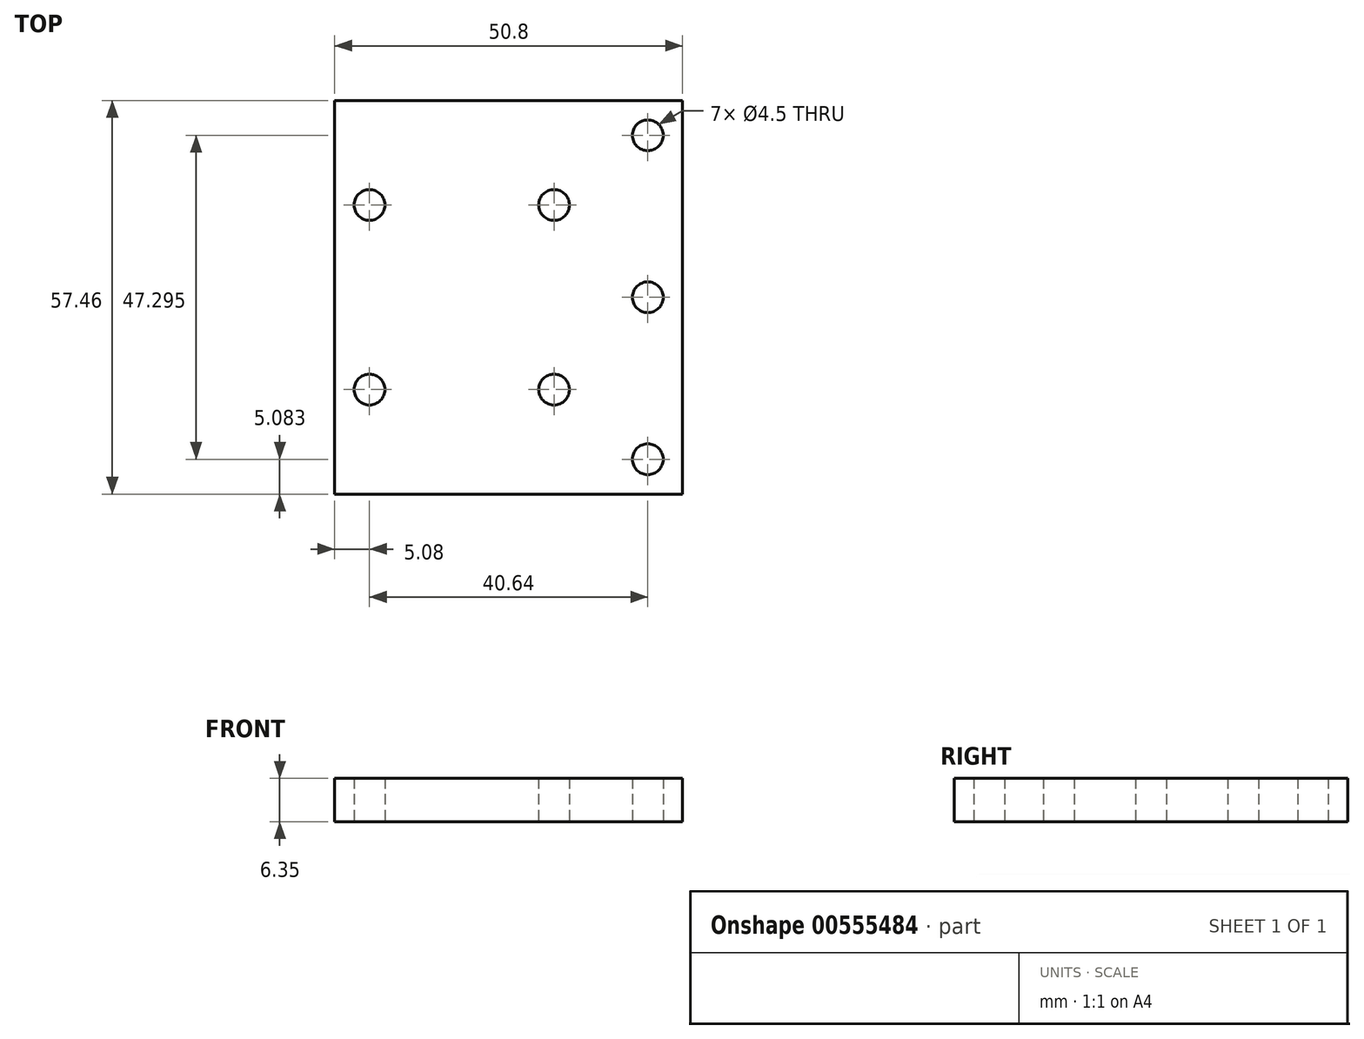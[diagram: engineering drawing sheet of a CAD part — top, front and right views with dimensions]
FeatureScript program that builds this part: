
annotation { "Feature Type Name" : "Feature", "Feature Type Description" : "" }
export const myFeature = defineFeature(function(context is Context, id is Id, definition is map)
    precondition{}
    {
        {
            var Q0;
            Q0=qCreatedBy(makeId("Top.planeOp"),FACE);
            var sketch = newSketch(context, id + "F0", { "sketchPlane" : qUnion([Q0])});
            skLineSegment(sketch, "E0.bottom", {"start": v(-25.4, 28.73) * mm, "end": v(25.4, 28.73) * mm});
            skLineSegment(sketch, "E0.top", {"start": v(-25.4, -28.73) * mm, "end": v(25.4, -28.73) * mm});
            skLineSegment(sketch, "E0.left", {"start": v(-25.4, 28.73) * mm, "end": v(-25.4, -28.73) * mm});
            skLineSegment(sketch, "E0.right", {"start": v(25.4, 28.73) * mm, "end": v(25.4, -28.73) * mm});
            skPoint(sketch, "E0.middle", {"position": v(0, 0) * mm});
            skLineSegment(sketch, "E1", {"start": v(-25.4, 13.47) * mm, "end": v(25.4, 13.47) * mm, "construction": true});
            skLineSegment(sketch, "E2", {"start": v(-20.32, 28.73) * mm, "end": v(-20.32, -28.73) * mm, "construction": true});
            skLineSegment(sketch, "E3", {"start": v(6.63, 28.73) * mm, "end": v(6.63, -28.73) * mm, "construction": true});
            skLineSegment(sketch, "E4", {"start": v(-25.4, -13.47) * mm, "end": v(25.4, -13.47) * mm, "construction": true});
            skLineSegment(sketch, "E5", {"start": v(-25.4, 0) * mm, "end": v(25.4, 0) * mm, "construction": true});
            skPoint(sketch, "E6", {"position": v(-20.32, -13.47) * mm});
            skPoint(sketch, "E7", {"position": v(-20.32, 13.47) * mm});
            skPoint(sketch, "E8", {"position": v(6.63, 13.47) * mm});
            skPoint(sketch, "E9", {"position": v(6.63, -13.47) * mm});
            skLineSegment(sketch, "E10", {"start": v(20.32, -28.73) * mm, "end": v(20.32, 28.73) * mm, "construction": true});
            skPoint(sketch, "E11", {"position": v(20.32, 0) * mm});
            skPoint(sketch, "E12", {"position": v(20.32, -23.65) * mm});
            skPoint(sketch, "E13", {"position": v(20.32, 23.65) * mm});
            skSolve(sketch);
        }
        {
            var Q0;
            {var subQ0=sQuery(id+"F0.wireOp",EDGE,"E0.right");Q0=makeQuery(id+"F0.imprint","IMPRINT",FACE,{"disambiguationData":[TD([[makeQuery(id+"F0.imprint","IMPRINT",EDGE,{"derivedFrom":subQ0}),-1.0]])]});}
            extrude(context, id + "F1", {"entities" : qUnion([Q0]), "depth" : 6.35 * mm, "offsetDistance" : 25.4 * mm});
        }
        {
            var Q0;
            Q0=sQuery(id+"F0.wireOp",VERTEX,"E6");
            var Q1;
            Q1=makeQuery(id+"F1.opExtrude","SWEPT_BODY",BODY,{"disambiguationData":[OSD([sQuery(id+"F0.wireOp",EDGE,"E0.bottom"),sQuery(id+"F0.wireOp",EDGE,"E0.top"),sQuery(id+"F0.wireOp",EDGE,"E0.right"),sQuery(id+"F0.wireOp",EDGE,"H2lXDhBS-bBmv-jnvt-dtpl-yNRelDX2eWJu")])]});
            hole(context, id + "F2", {"style" : HoleStyle.SIMPLE, "endStyle" : HoleEndStyle.THROUGH, "oppositeDirection" : true, "standardTappedOrClearance" : lookupTablePath({ "standard" : "ANSI", "fit" : "Normal (ASME)", "size" : "#8", "type" : "Clearance" }), "standardBlindInLast" : lookupTablePath({ "fit" : "Free", "standard" : "ANSI", "size" : "#8", "type" : "Clearance" }), "holeDiameter" : 4.5 * mm, "isTappedThrough" : true, "tappedDepth" : 12.7 * mm, "tapClearance" : 3, "locations" : qUnion([Q0]), "scope" : qUnion([Q1])});
        }
        {
            var Q0;
            Q0=sQuery(id+"F0.wireOp",VERTEX,"E7");
            var Q1;
            Q1=makeQuery(id+"F1.opExtrude","SWEPT_BODY",BODY,{"disambiguationData":[OSD([sQuery(id+"F0.wireOp",EDGE,"E0.bottom"),sQuery(id+"F0.wireOp",EDGE,"E0.top"),sQuery(id+"F0.wireOp",EDGE,"E0.right"),sQuery(id+"F0.wireOp",EDGE,"H2lXDhBS-bBmv-jnvt-dtpl-yNRelDX2eWJu")])]});
            hole(context, id + "F3", {"style" : HoleStyle.SIMPLE, "endStyle" : HoleEndStyle.THROUGH, "oppositeDirection" : true, "standardTappedOrClearance" : lookupTablePath({ "standard" : "ANSI", "fit" : "Normal (ASME)", "size" : "#8", "type" : "Clearance" }), "standardBlindInLast" : lookupTablePath({ "fit" : "Free", "standard" : "ANSI", "size" : "#8", "type" : "Clearance" }), "holeDiameter" : 4.5 * mm, "isTappedThrough" : true, "tappedDepth" : 12.7 * mm, "tapClearance" : 3, "locations" : qUnion([Q0]), "scope" : qUnion([Q1])});
        }
        {
            var Q0;
            Q0=sQuery(id+"F0.wireOp",VERTEX,"E8");
            var Q1;
            Q1=makeQuery(id+"F1.opExtrude","SWEPT_BODY",BODY,{"disambiguationData":[OSD([sQuery(id+"F0.wireOp",EDGE,"E0.bottom"),sQuery(id+"F0.wireOp",EDGE,"E0.top"),sQuery(id+"F0.wireOp",EDGE,"E0.right"),sQuery(id+"F0.wireOp",EDGE,"H2lXDhBS-bBmv-jnvt-dtpl-yNRelDX2eWJu")])]});
            hole(context, id + "F4", {"style" : HoleStyle.SIMPLE, "endStyle" : HoleEndStyle.THROUGH, "oppositeDirection" : true, "standardTappedOrClearance" : lookupTablePath({ "standard" : "ANSI", "fit" : "Normal (ASME)", "size" : "#8", "type" : "Clearance" }), "standardBlindInLast" : lookupTablePath({ "fit" : "Free", "standard" : "ANSI", "size" : "#8", "type" : "Clearance" }), "holeDiameter" : 4.5 * mm, "isTappedThrough" : true, "tappedDepth" : 12.7 * mm, "tapClearance" : 3, "locations" : qUnion([Q0]), "scope" : qUnion([Q1])});
        }
        {
            var Q0;
            Q0=sQuery(id+"F0.wireOp",VERTEX,"E9");
            var Q1;
            Q1=makeQuery(id+"F1.opExtrude","SWEPT_BODY",BODY,{"disambiguationData":[OSD([sQuery(id+"F0.wireOp",EDGE,"E0.bottom"),sQuery(id+"F0.wireOp",EDGE,"E0.top"),sQuery(id+"F0.wireOp",EDGE,"E0.right"),sQuery(id+"F0.wireOp",EDGE,"H2lXDhBS-bBmv-jnvt-dtpl-yNRelDX2eWJu")])]});
            hole(context, id + "F5", {"style" : HoleStyle.SIMPLE, "endStyle" : HoleEndStyle.THROUGH, "oppositeDirection" : true, "standardTappedOrClearance" : lookupTablePath({ "standard" : "ANSI", "fit" : "Normal (ASME)", "size" : "#8", "type" : "Clearance" }), "standardBlindInLast" : lookupTablePath({ "fit" : "Free", "standard" : "ANSI", "size" : "#8", "type" : "Clearance" }), "holeDiameter" : 4.5 * mm, "isTappedThrough" : true, "tappedDepth" : 12.7 * mm, "tapClearance" : 3, "locations" : qUnion([Q0]), "scope" : qUnion([Q1])});
        }
        {
            var Q0;
            Q0=sQuery(id+"F0.wireOp",VERTEX,"E12");
            var Q1;
            Q1=makeQuery(id+"F1.opExtrude","SWEPT_BODY",BODY,{"disambiguationData":[OSD([sQuery(id+"F0.wireOp",EDGE,"E0.bottom"),sQuery(id+"F0.wireOp",EDGE,"E0.top"),sQuery(id+"F0.wireOp",EDGE,"E0.left"),sQuery(id+"F0.wireOp",EDGE,"E0.right")])]});
            hole(context, id + "F6", {"style" : HoleStyle.SIMPLE, "endStyle" : HoleEndStyle.THROUGH, "oppositeDirection" : true, "standardTappedOrClearance" : lookupTablePath({ "standard" : "ANSI", "fit" : "Normal (ASME)", "size" : "#8", "type" : "Clearance" }), "standardBlindInLast" : lookupTablePath({ "fit" : "Free", "standard" : "ANSI", "size" : "#8", "type" : "Clearance" }), "holeDiameter" : 4.5 * mm, "isTappedThrough" : true, "tappedDepth" : 12.7 * mm, "tapClearance" : 3, "locations" : qUnion([Q0]), "scope" : qUnion([Q1])});
        }
        {
            var Q0;
            Q0=sQuery(id+"F0.wireOp",VERTEX,"E11");
            var Q1;
            Q1=makeQuery(id+"F1.opExtrude","SWEPT_BODY",BODY,{"disambiguationData":[OSD([sQuery(id+"F0.wireOp",EDGE,"E0.bottom"),sQuery(id+"F0.wireOp",EDGE,"E0.top"),sQuery(id+"F0.wireOp",EDGE,"E0.left"),sQuery(id+"F0.wireOp",EDGE,"E0.right")])]});
            hole(context, id + "F7", {"style" : HoleStyle.SIMPLE, "endStyle" : HoleEndStyle.THROUGH, "oppositeDirection" : true, "standardTappedOrClearance" : lookupTablePath({ "standard" : "ANSI", "fit" : "Normal (ASME)", "size" : "#8", "type" : "Clearance" }), "standardBlindInLast" : lookupTablePath({ "fit" : "Free", "standard" : "ANSI", "size" : "#8", "type" : "Clearance" }), "holeDiameter" : 4.5 * mm, "isTappedThrough" : true, "tappedDepth" : 12.7 * mm, "tapClearance" : 3, "locations" : qUnion([Q0]), "scope" : qUnion([Q1])});
        }
        {
            var Q0;
            Q0=sQuery(id+"F0.wireOp",VERTEX,"E13");
            var Q1;
            Q1=makeQuery(id+"F1.opExtrude","SWEPT_BODY",BODY,{"disambiguationData":[OSD([sQuery(id+"F0.wireOp",EDGE,"E0.bottom"),sQuery(id+"F0.wireOp",EDGE,"E0.top"),sQuery(id+"F0.wireOp",EDGE,"E0.left"),sQuery(id+"F0.wireOp",EDGE,"E0.right")])]});
            hole(context, id + "F8", {"style" : HoleStyle.SIMPLE, "endStyle" : HoleEndStyle.THROUGH, "oppositeDirection" : true, "standardTappedOrClearance" : lookupTablePath({ "standard" : "ANSI", "fit" : "Normal (ASME)", "size" : "#8", "type" : "Clearance" }), "standardBlindInLast" : lookupTablePath({ "fit" : "Free", "standard" : "ANSI", "size" : "#8", "type" : "Clearance" }), "holeDiameter" : 4.5 * mm, "isTappedThrough" : true, "tappedDepth" : 12.7 * mm, "tapClearance" : 3, "locations" : qUnion([Q0]), "scope" : qUnion([Q1])});
        }
    });
